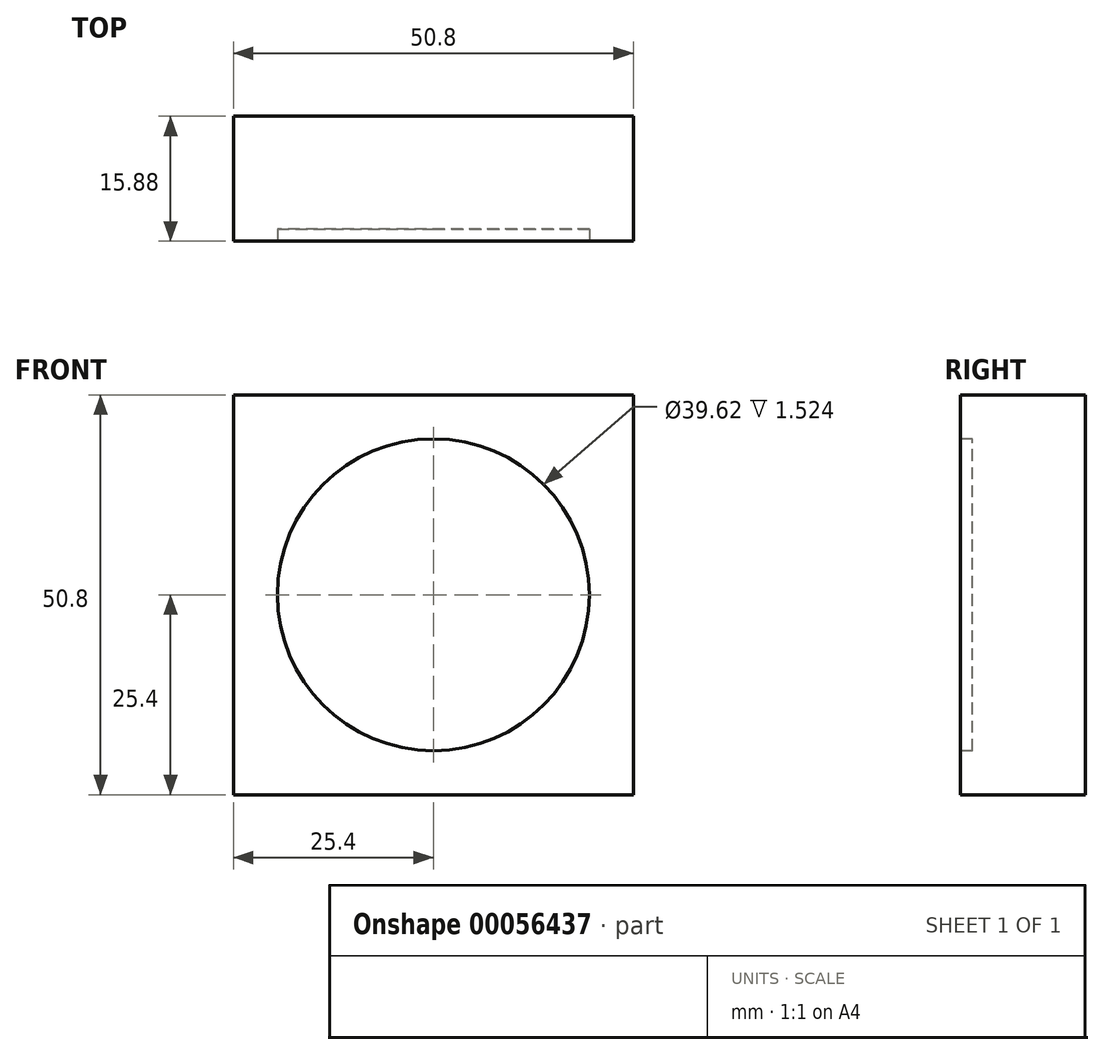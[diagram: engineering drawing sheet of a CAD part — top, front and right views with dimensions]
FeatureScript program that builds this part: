
annotation { "Feature Type Name" : "Feature", "Feature Type Description" : "" }
export const myFeature = defineFeature(function(context is Context, id is Id, definition is map)
    precondition{}
    {
        {
            var Q0;
            Q0=qCreatedBy(makeId("Front.planeOp"),FACE);
            var sketch = newSketch(context, id + "F0", { "sketchPlane" : qUnion([Q0])});
            skLineSegment(sketch, "E0.rect.bottom", {"start": v(25.4, 25.4) * mm, "end": v(-25.4, 25.4) * mm});
            skLineSegment(sketch, "E0.rect.top", {"start": v(25.4, -25.4) * mm, "end": v(-25.4, -25.4) * mm});
            skLineSegment(sketch, "E0.rect.left", {"start": v(25.4, 25.4) * mm, "end": v(25.4, -25.4) * mm});
            skLineSegment(sketch, "E0.rect.right", {"start": v(-25.4, 25.4) * mm, "end": v(-25.4, -25.4) * mm});
            skPoint(sketch, "E0.rect.middle", {"position": v(0, 0) * mm});
            skSolve(sketch);
        }
        {
            var Q0;
            Q0=makeQuery(id+"F0.imprint","IMPRINT",FACE,{"disambiguationData":[TD([[makeQuery(id+"F0.imprint","IMPRINT",EDGE,{"derivedFrom":sQuery(id+"F0.wireOp",EDGE,"E0.rect.bottom")}),1.0]])]});
            extrude(context, id + "F1", {"entities" : qUnion([Q0]), "depth" : 15.88 * mm});
        }
        {
            var Q0;
            Q0=makeQuery(id+"F1.opExtrude","CAP_FACE",FACE,{"disambiguationData":[OSD([sQuery(id+"F0.wireOp",EDGE,"E0.rect.bottom"),sQuery(id+"F0.wireOp",EDGE,"E0.rect.top"),sQuery(id+"F0.wireOp",EDGE,"E0.rect.left"),sQuery(id+"F0.wireOp",EDGE,"E0.rect.right")])],"isStart":false});
            var sketch = newSketch(context, id + "F2", { "sketchPlane" : qUnion([Q0])});
            skCircle(sketch, "E1", {"center": v(0, 0) * mm, "radius": 19.81 * mm});
            skSolve(sketch);
        }
        {
            var Q0;
            Q0 = qSketchRegion(id + "F2", true);
            extrude(context, id + "F3", {"entities" : qUnion([Q0]), "operationType" : NewBodyOperationType.REMOVE, "oppositeDirection" : true, "depth" : 1.52 * mm});
        }
    });
